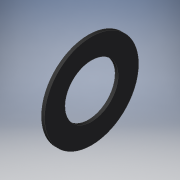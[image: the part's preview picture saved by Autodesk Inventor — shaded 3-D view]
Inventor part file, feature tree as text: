
AUTODESK INVENTOR PART (.ipt)
format: ipt  version: 2019 (Build 230136000, 136)  size: 117,248 bytes
history: native  units: mm
features: other x14, revolve x1, sketch x1
ambient origin geometry x8: Origin, YZ Plane, XZ Plane, XY Plane, X Axis, Y Axis, Z Axis, Center Point
bodies: Solid1 (feature_tree)
feature tree (16):
  revolve  "Revolution1"  [1 undecoded]
  other  "washer1_XY"
  other  "washer1_YZ"
  other  "washer1_ZX"
  other  "washer1_X"
  other  "washer1_Y"
  other  "washer1_Z"
  other  "washer1_Center"
  other  "washer2_XY"
  other  "washer2_YZ"
  other  "washer2_ZX"
  other  "washer2_X"
  other  "washer2_Y"
  other  "washer2_Z"
  other  "washer2_Center"
  sketch  "Sketch_1"  dims[d0=360.0deg]
note: 1 required parameter value undecoded (feature->parameter linkage not recoverable at this tier; creation-order binding heuristic only, values carry confidence <= 0.55)
